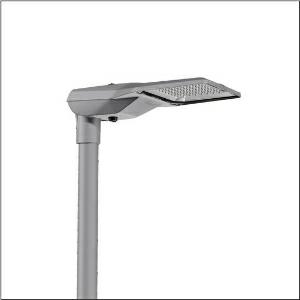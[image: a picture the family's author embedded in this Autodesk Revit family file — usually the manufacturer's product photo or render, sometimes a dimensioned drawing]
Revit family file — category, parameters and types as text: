
# Revit family: streetlight_sl_21_midi___p0_8ab_5xe3r33t08mb_ae32
name_source: partatom
category: Lighting Fixtures
units: mm (PartAtom-declared; Revit-internal decimal feet)

## family parameters
Cut with Voids When Loaded = No
Host = Face
Light Source = No
Part Type = Normal
Room Calculation Point = No
Round Connector Dimension = Use Diameter
Shared = No

## types (1)
- --- (1 x LED, 15870 lm, 136 W, 3000K)
    Apparent Load = 136 VA
    CIE Flux Codes = 36 71 98 100 100
    Color Rendering = 70
    Color Temperature = 3000K
    Default Elevation = 1800 mm
    Description = Streetlight SL 21 midi, mast luminaire, primary light control with lens, of PMMA, primary optical cover: cover, of toughened safety glass, transparent, light distribution: P0.8aB, light emission: direct distribution, primary light characteristic: asymmetric, installation type: post-top, side-entry, LED, High Power LED, rated luminous flux: 15.870lm, luminous efficacy: 117lm/W, light colour: 730, colour temperature: 3000K, control gear: D4i, control: pre-setting: logarithmic dimming characteristic, flexible luminous flux parameterisation, time-dependent luminous flux control, constant luminous flux control, overheat protection, mains connection: 230..240V, AC, 50/60Hz, start of lifetime: 136W, end of service life: 142W, reduction: 61W, luminaire housing, of diecast aluminium, powder-coated, SITECO metallic grey (DB 702S), corrosivity category C5 high according to DIN EN ISO 12944, multi-level sealing system, sealing non-destructively replaceable, inclination adjustable: 0°, 5°, 10°, 15°, please order mast flange separately, length: 644mm, width: 335mm, height: 110mm, mast flange for spigot size: 42mm (side-entry): 5XC10008XM4, 60/48mm (side-entry/post-top): 5XC10108XM2, 76/60mm (side-entry/post-top): 5XC10108XM1, mounting height: 4..8m, Smart Interface below and above, protection rating (complete): IP66, insulation class (complete): insulation class II (safety insulation), certification: CE, ENEC, ENEC+, VDE, impact resistance: IK10, permissible operating ambient temperature for outdoor applications: -40..+50°C, standard-compliant lighting for roads and squares, packaging unit: 1 piece

Light Distribution: P0.8aB
    Height = 111 mm
    Lamp = 1 x LED
    Lamp Light Flux = 15870 lm
    Lamp Power = 136 W
    Lamp count = 1
    Length = 644 mm
    Luminous efficacy = 117 lm/W
    Manufacturer = Siteco
    ModVariant = No
    Model = 5XE3R33T08MB
    Number of Poles = 1
    OnlyDefault = Yes
    Power Factor = 1
    Product Name = Streetlight SL 21 midi | P0.8aB
    Product group = mast luminaire | pylon top
    ProductGroupID = 6100
    Protection Class = Protection class II
    Protection Degree = IP 66
    RLX_Detail_Level = 1
    RLX_Emergency_Light_Flux = 0 lm
    RLX_Emergency_Type = 0
    RLX_Emergency_Type_DB = No
    RlxData = <blob elided: 90721 chars, md5=cd9d12f6>
    Socket = socket
    Standby Power = 0 W
    System Light Flux = 15870 lm
    System Power = 136 W
    Type Comments = factory setting: luminous flux: 100 % | dim-lin: 254 | 695 mA
    Type Image = l_1004304.jpg
    URL = http://relux.com
    VarID = @adj_082709
    Voltage = 0 V
    Weight = 0.00 kg
    Width = 336 mm

## geometry (parser evidence)
native form markers: Blend x4, Sweep x12
no freeform markers — native parametric forms only
